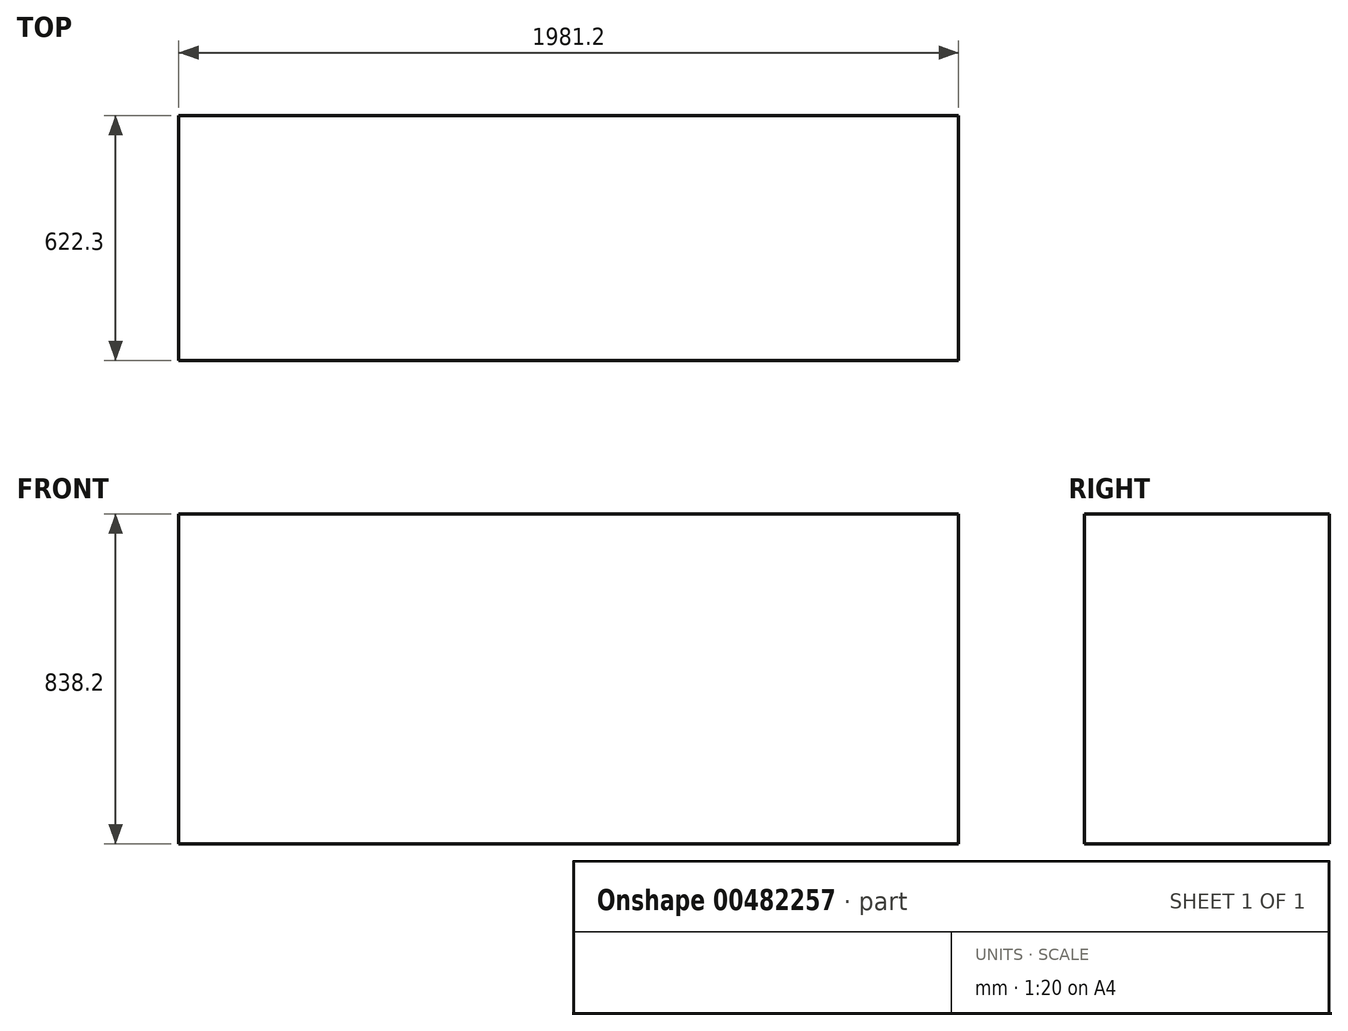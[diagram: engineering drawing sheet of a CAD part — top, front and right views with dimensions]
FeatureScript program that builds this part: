
annotation { "Feature Type Name" : "Feature", "Feature Type Description" : "" }
export const myFeature = defineFeature(function(context is Context, id is Id, definition is map)
    precondition{}
    {
        {
            var Q0;
            Q0=qCreatedBy(makeId("Right.planeOp"),FACE);
            var sketch = newSketch(context, id + "F0", { "sketchPlane" : qUnion([Q0])});
            skLineSegment(sketch, "E0.bottom", {"start": v(0, 0) * mm, "end": v(-622.3, 0) * mm});
            skLineSegment(sketch, "E0.top", {"start": v(0, 838.2) * mm, "end": v(-622.3, 838.2) * mm});
            skLineSegment(sketch, "E0.left", {"start": v(0, 0) * mm, "end": v(0, 838.2) * mm});
            skLineSegment(sketch, "E0.right", {"start": v(-622.3, 0) * mm, "end": v(-622.3, 838.2) * mm});
            skLineSegment(sketch, "E1.bottom", {"start": v(-622.3, 838.2) * mm, "end": v(-177.8, 838.2) * mm});
            skLineSegment(sketch, "E1.top", {"start": v(-622.3, 1117.6) * mm, "end": v(-177.8, 1117.6) * mm});
            skLineSegment(sketch, "E1.left", {"start": v(-622.3, 838.2) * mm, "end": v(-622.3, 1117.6) * mm});
            skLineSegment(sketch, "E1.right", {"start": v(-177.8, 838.2) * mm, "end": v(-177.8, 1117.6) * mm});
            skSolve(sketch);
        }
        {
            var Q0;
            Q0=makeQuery(id+"F0.imprint","IMPRINT",FACE,{"disambiguationData":[TD([[makeQuery(id+"F0.imprint","IMPRINT",EDGE,{"derivedFrom":sQuery(id+"F0.wireOp",EDGE,"E1.bottom")}),1.0]])]});
            var Q1;
            Q1=makeQuery(id+"F0.imprint","IMPRINT",FACE,{"disambiguationData":[TD([[makeQuery(id+"F0.imprint","IMPRINT",EDGE,{"derivedFrom":sQuery(id+"F0.wireOp",EDGE,"E0.bottom")}),-1.0]])]});
            extrude(context, id + "F1", {"entities" : qUnion([Q0, Q1]), "depth" : 1981.2 * mm});
        }
    });
